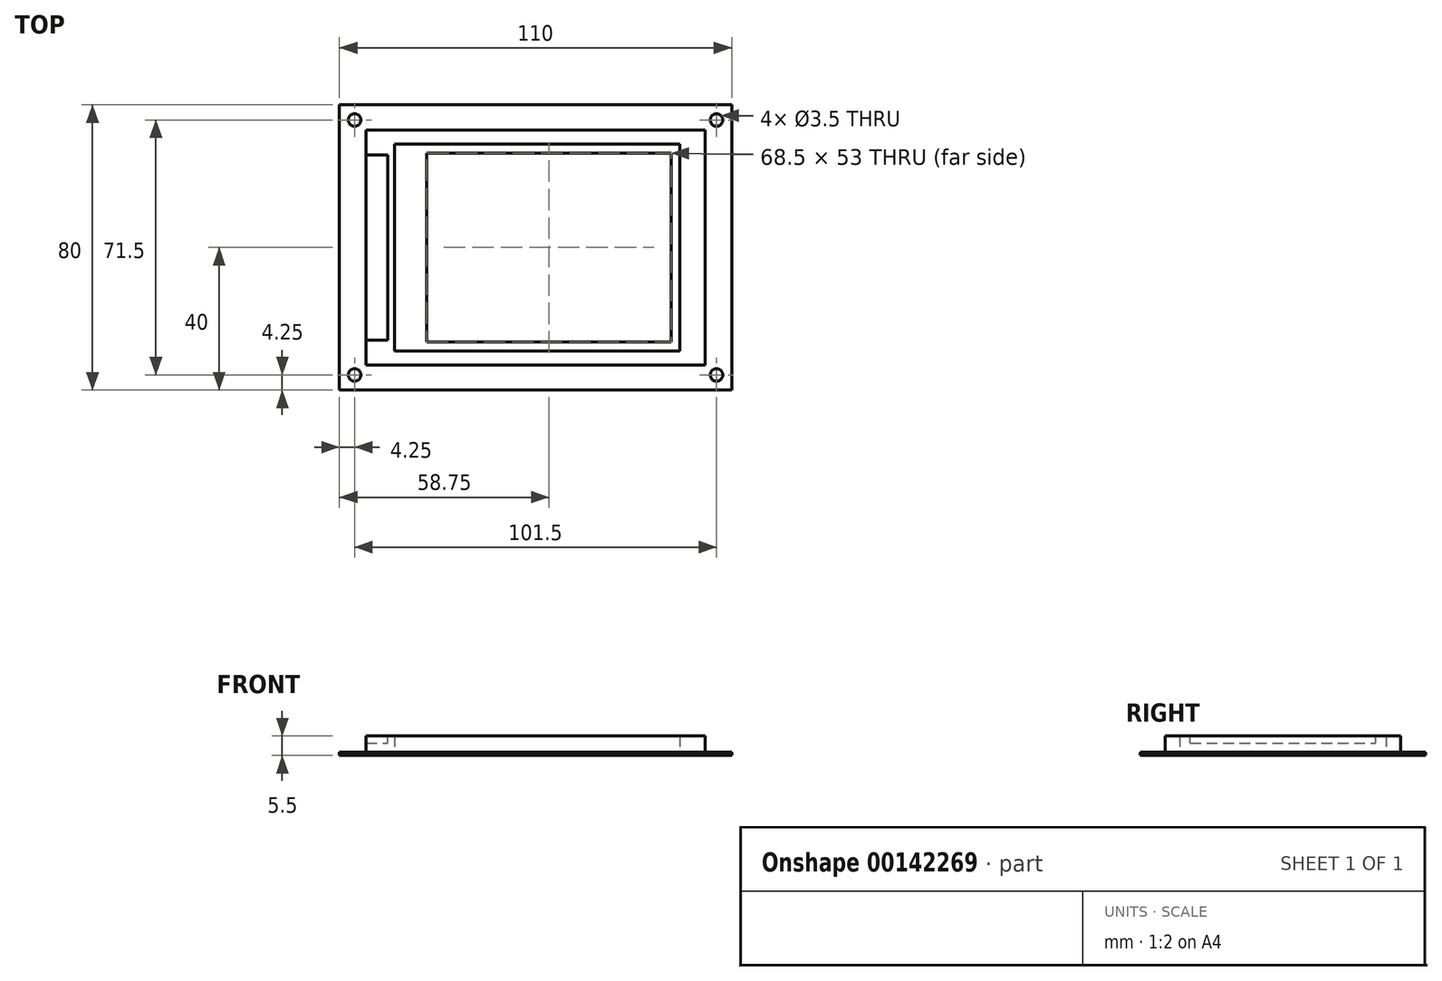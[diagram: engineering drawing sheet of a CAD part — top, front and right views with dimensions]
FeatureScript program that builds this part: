
annotation { "Feature Type Name" : "Feature", "Feature Type Description" : "" }
export const myFeature = defineFeature(function(context is Context, id is Id, definition is map)
    precondition{}
    {
        {
            var Q0;
            Q0=qCreatedBy(makeId("Top.planeOp"),FACE);
            var sketch = newSketch(context, id + "F0", { "sketchPlane" : qUnion([Q0])});
            skLineSegment(sketch, "E0.bottom", {"start": v(-40, 29) * mm, "end": v(40, 29) * mm});
            skLineSegment(sketch, "E0.top", {"start": v(-40, -29) * mm, "end": v(40, -29) * mm});
            skLineSegment(sketch, "E0.left", {"start": v(-40, 29) * mm, "end": v(-40, -29) * mm});
            skLineSegment(sketch, "E0.right", {"start": v(40, 29) * mm, "end": v(40, -29) * mm});
            skPoint(sketch, "E0.middle", {"position": v(0, 0) * mm});
            skLineSegment(sketch, "E1.bottom", {"start": v(-48, 33) * mm, "end": v(47, 33) * mm});
            skLineSegment(sketch, "E2.MirrorCS", {"start": v(-48, -33) * mm, "end": v(47, -33) * mm});
            skLineSegment(sketch, "E3", {"start": v(47, 33) * mm, "end": v(47, -33) * mm});
            skLineSegment(sketch, "E4", {"start": v(-48, -33) * mm, "end": v(-48, 33) * mm});
            skLineSegment(sketch, "E5.0", {"start": v(-60, 49) * mm, "end": v(-60, -49) * mm, "construction": true});
            skLineSegment(sketch, "E5.1", {"start": v(-60, 49) * mm, "end": v(60, 49) * mm, "construction": true});
            skLineSegment(sketch, "E5.2", {"start": v(60, 49) * mm, "end": v(60, -49) * mm, "construction": true});
            skLineSegment(sketch, "E5.3", {"start": v(-60, -49) * mm, "end": v(60, -49) * mm, "construction": true});
            skLineSegment(sketch, "E6.bottom", {"start": v(-31, 26.5) * mm, "end": v(37.5, 26.5) * mm});
            skLineSegment(sketch, "E6.top", {"start": v(-31, -26.5) * mm, "end": v(37.5, -26.5) * mm});
            skLineSegment(sketch, "E6.right", {"start": v(37.5, 26.5) * mm, "end": v(37.5, -26.5) * mm});
            skLineSegment(sketch, "E7", {"start": v(-31, 26.5) * mm, "end": v(-31, -26.5) * mm});
            skSolve(sketch);
        }
        {
            var Q0;
            Q0 = qSketchRegion(id + "F0", true);
            var Q1;
            Q1=makeQuery(id+"F0.imprint","IMPRINT",FACE,{"disambiguationData":[TD([[makeQuery(id+"F0.imprint","IMPRINT",EDGE,{"derivedFrom":sQuery(id+"F0.wireOp",EDGE,"E0.bottom")}),-1.0]])]});
            extrude(context, id + "F1", {"entities" : qUnion([Q0, Q1]), "depth" : 0.1 * mm});
        }
        {
            var Q0;
            Q0=makeQuery(id+"F0.imprint","IMPRINT",FACE,{"disambiguationData":[TD([[makeQuery(id+"F0.imprint","IMPRINT",EDGE,{"derivedFrom":sQuery(id+"F0.wireOp",EDGE,"E0.bottom")}),1.0]])]});
            extrude(context, id + "F2", {"entities" : qUnion([Q0]), "operationType" : NewBodyOperationType.ADD, "depth" : 4.5 * mm});
        }
        {
            var Q0;
            Q0=makeQuery(id+"F2.opExtrude","CAP_FACE",FACE,{"disambiguationData":[OSD([sQuery(id+"F0.wireOp",EDGE,"E0.bottom"),sQuery(id+"F0.wireOp",EDGE,"E0.top"),sQuery(id+"F0.wireOp",EDGE,"E0.left"),sQuery(id+"F0.wireOp",EDGE,"E0.right"),sQuery(id+"F0.wireOp",EDGE,"E1.bottom"),sQuery(id+"F0.wireOp",EDGE,"E2.MirrorCS"),sQuery(id+"F0.wireOp",EDGE,"E3"),sQuery(id+"F0.wireOp",EDGE,"E4")])],"isStart":false});
            var sketch = newSketch(context, id + "F3", { "sketchPlane" : qUnion([Q0])});
            skLineSegment(sketch, "E8.bottom", {"start": v(-48, 26) * mm, "end": v(-42, 26) * mm});
            skLineSegment(sketch, "E8.top", {"start": v(-48, -26) * mm, "end": v(-42, -26) * mm});
            skLineSegment(sketch, "E8.left", {"start": v(-48, 26) * mm, "end": v(-48, -26) * mm});
            skLineSegment(sketch, "E8.right", {"start": v(-42, 26) * mm, "end": v(-42, -26) * mm});
            skSolve(sketch);
        }
        {
            var Q0;
            Q0 = qSketchRegion(id + "F3", true);
            extrude(context, id + "F4", {"entities" : qUnion([Q0]), "operationType" : NewBodyOperationType.REMOVE, "oppositeDirection" : true, "depth" : 2 * mm});
        }
        {
            var Q0;
            Q0=makeQuery(id+"F1.opExtrude","CAP_FACE",FACE,{"disambiguationData":[OSD([sQuery(id+"F0.wireOp",EDGE,"E1.bottom"),sQuery(id+"F0.wireOp",EDGE,"E2.MirrorCS"),sQuery(id+"F0.wireOp",EDGE,"E3"),sQuery(id+"F0.wireOp",EDGE,"E4"),sQuery(id+"F0.wireOp",EDGE,"E6.bottom"),sQuery(id+"F0.wireOp",EDGE,"E6.top"),sQuery(id+"F0.wireOp",EDGE,"E6.right"),sQuery(id+"F0.wireOp",EDGE,"E7")])],"isStart":true});
            var sketch = newSketch(context, id + "F5", { "sketchPlane" : qUnion([Q0])});
            skLineSegment(sketch, "E9.0.0", {"start": v(47, 33) * mm, "end": v(-48, 33) * mm});
            skLineSegment(sketch, "E9.0.1", {"start": v(-48, 33) * mm, "end": v(-48, -33) * mm});
            skLineSegment(sketch, "E9.0.2", {"start": v(-48, -33) * mm, "end": v(47, -33) * mm});
            skLineSegment(sketch, "E9.0.3", {"start": v(47, -33) * mm, "end": v(47, 33) * mm});
            skLineSegment(sketch, "E10.0", {"start": v(-28, -17) * mm, "end": v(28, -17) * mm, "construction": true});
            skLineSegment(sketch, "E10.1", {"start": v(-28, -17) * mm, "end": v(-28, 17) * mm, "construction": true});
            skLineSegment(sketch, "E10.2", {"start": v(-28, 17) * mm, "end": v(28, 17) * mm, "construction": true});
            skLineSegment(sketch, "E10.3", {"start": v(28, -17) * mm, "end": v(28, 17) * mm, "construction": true});
            skPoint(sketch, "E11", {"position": v(-0.5, 33) * mm});
            skLineSegment(sketch, "E12", {"start": v(-0.5, 33) * mm, "end": v(-0.5, 13.17) * mm, "construction": true});
            skPoint(sketch, "E13", {"position": v(-48, 0) * mm});
            skLineSegment(sketch, "E14", {"start": v(-48, 0) * mm, "end": v(-40.19, 0) * mm, "construction": true});
            skLineSegment(sketch, "E15.bottom", {"start": v(-55.5, 40) * mm, "end": v(54.5, 40) * mm});
            skLineSegment(sketch, "E15.top", {"start": v(-55.5, -40) * mm, "end": v(54.5, -40) * mm});
            skLineSegment(sketch, "E15.left", {"start": v(-55.5, 40) * mm, "end": v(-55.5, -40) * mm});
            skLineSegment(sketch, "E15.right", {"start": v(54.5, 40) * mm, "end": v(54.5, -40) * mm});
            skLineSegment(sketch, "E16", {"start": v(0, 0) * mm, "end": v(0, 8.2) * mm, "construction": true});
            skPoint(sketch, "E17", {"position": v(-0.5, 40) * mm});
            skLineSegment(sketch, "E18", {"start": v(-0.5, 40) * mm, "end": v(-0.5, 20.96) * mm, "construction": true});
            skPoint(sketch, "E19", {"position": v(-55.5, 0) * mm});
            skLineSegment(sketch, "E20", {"start": v(-55.5, 0) * mm, "end": v(-65.1, 0) * mm, "construction": true});
            skCircle(sketch, "E21", {"center": v(-51.25, 35.75) * mm, "radius": 1.75 * mm});
            skCircle(sketch, "E22.MirrorC", {"center": v(50.25, 35.75) * mm, "radius": 1.75 * mm});
            skCircle(sketch, "E23.MirrorC", {"center": v(-51.25, -35.75) * mm, "radius": 1.75 * mm});
            skCircle(sketch, "E24.MirrorC", {"center": v(50.25, -35.75) * mm, "radius": 1.75 * mm});
            skSolve(sketch);
        }
        {
            var Q0;
            Q0=makeQuery(id+"F5.imprint","IMPRINT",FACE,{"disambiguationData":[TD([[makeQuery(id+"F5.imprint","IMPRINT",EDGE,{"derivedFrom":sQuery(id+"F5.wireOp",EDGE,"E9.0.0")}),-1.0]])]});
            var Q1;
            Q1=makeQuery(id+"F5.imprint","IMPRINT",FACE,{"disambiguationData":[TD([[makeQuery(id+"F5.imprint","IMPRINT",EDGE,{"derivedFrom":sQuery(id+"F5.wireOp",EDGE,"E9.0.0")}),1.0]])]});
            extrude(context, id + "F6", {"entities" : qUnion([Q0, Q1]), "operationType" : NewBodyOperationType.ADD, "depth" : 1 * mm});
        }
    });
